# Revit family: 571822730004(2022)
name_source: partatom
category: Plumbing Fixtures
revit_build: Autodesk Revit 2018 (Build: 20170223_1515(x64)
units: mm (PartAtom-declared; Revit-internal decimal feet)

## family parameters
Always vertical = Yes
Cut with Voids When Loaded = No
OmniClass Number = 23.45.55.00
OmniClass Title = Sanitary Faucets, Wastes
Part Type = Normal
Room Calculation Point = No
Round Connector Dimension = Use Diameter
Shared = No
Work Plane-Based = No

## types (1)
- 571822730004 Washbasin faucet
    2D/3D/BIM Files URL = http://static.hansa.com
    3D View = https://static.hansa.com
    Advanced Features = Inner body made of DZR brass
    Aerator = PCA® - constant flow rate regardless of pressure variations
    Approval ABP = PA-IX 38025/IO
    AssetType = Fixed
    BIMObjectName = 571822730004(2022)
    Backflow Prevention EN1717 = AA
    BodyMaterial = Brass
    Brand = HANSA
    Catalog Drawing URL = http://static.hansa.com
    CloseOffRating = 0
    Color = Chrome
    Connection = Flexible inlet pipes
    Connection Size = G3/8
    Dimension Drawing URL = http://static.hansa.com
    DurationUnit = Year
    EAN Number = 4057304018244
    EN Standard = EN 817
    ETIM Class Number = EC011328 Washbasin mixing tap
    Extensions = Push pop-up waste without draw-rod
    FDV Document URL = http://www.hansa.com
    FaucetMainMaterial = Brass
    Features = Single-lever
    Finish = Polished
    Flow Drawing URL = http://static.hansa.com
    Flow Rate At 300kPa With Flow Controller = 0.6 L/s
    FlowCoefficient = 0
    Group = Washbasin faucet
    IfcExportAs = IfcValveType
    IfcExportType = FAUCET
    InletConnectionSize = 10 mm  [stored 0.0328084 ft]
    Installation Type = Deck mounted
    Installation and Maintenance Guide URL = http://static.hansa.com
    Interactive AR View URL = https://static.hansa.com
    Lever Handle = Single operating lever/handle;Hot/Cold symbols
    Manufacturer = HANSA
    ManufacturerName = HANSA
    ManufacturerURL = http://www.hansa.com
    Market = International;Germany;Austria;Belgium;Netherlands;Czech Republic;Slovakia;Italy
    Material = Brass
    Max. Hot Water Supply = 70 °C
    Mechanical Parts = ø 25 mm ceramic cartridge for flow and temperature control
    Mobile Product Information URL = http://mpi.hansa.com
    Model = 571822730004 Washbasin faucet
    ModelReference = 571822730004
    Mounting Holes = 1 hole
    NBSDescription = Water supply fittings for wash basins and troughs
    NBSReference = 45-35-70/371
    Name = 571822730004 Washbasin faucet
    Name_en = 571822730004 Washbasin faucet
    Noise Class = I (ISO 3822)
    NominalDepth = 162 mm
    NominalHeight = 181 mm
    NominalWidth = 53 mm
    Product Code = 571822730004
    Product Family = HANSASTELA Eco
    Product Image URL = http://static.hansa.com
    Product URL = http://static.hansa.com
    ProductInformation = Kitchen faucet with high spout.
    Revision = 2
    Sales Package dimensions (LxWxH) = 673 x 195 x 81
    Shape = Sculptured
    Size = 55x160x180 mm
    Spare-Part Information URL = http://static.hansa.com
    Spout Projection = 106 mm
    Spout Type = Fixed spout
    Surface treatment = Chrome
    Technical DataSheet URL = http://www.hansa.com
    UNSPSC Class Number = 30181700 Faucets or taps
    URL ABP = http://static.hansa.com
    URL Declaration of Conformity = http://static.hansa.com
    URL REACH = http://static.hansa.com
    Uniclass2 = Pr_40_30_96_96
    Uniclass2015Description = Washbasin manual water supply sets
    Uniclass2015Reference = Pr_40_20_87_96
    Version = 2
    VersionDate = 01/07/2022
    Warranty Information URL = http://warranty.hansa.com
    WarrantyDescription = http://warranty.hansa.com
    WarrantyDurationUnit = Year
    Working Pressure = 50 - 1000 kPa

note: [stored X ft] marks values corroborated as IEEE doubles in the binary element streams (Revit-internal decimal feet)

## geometry (parser evidence)
native form markers: Sweep x4
no freeform markers — native parametric forms only
